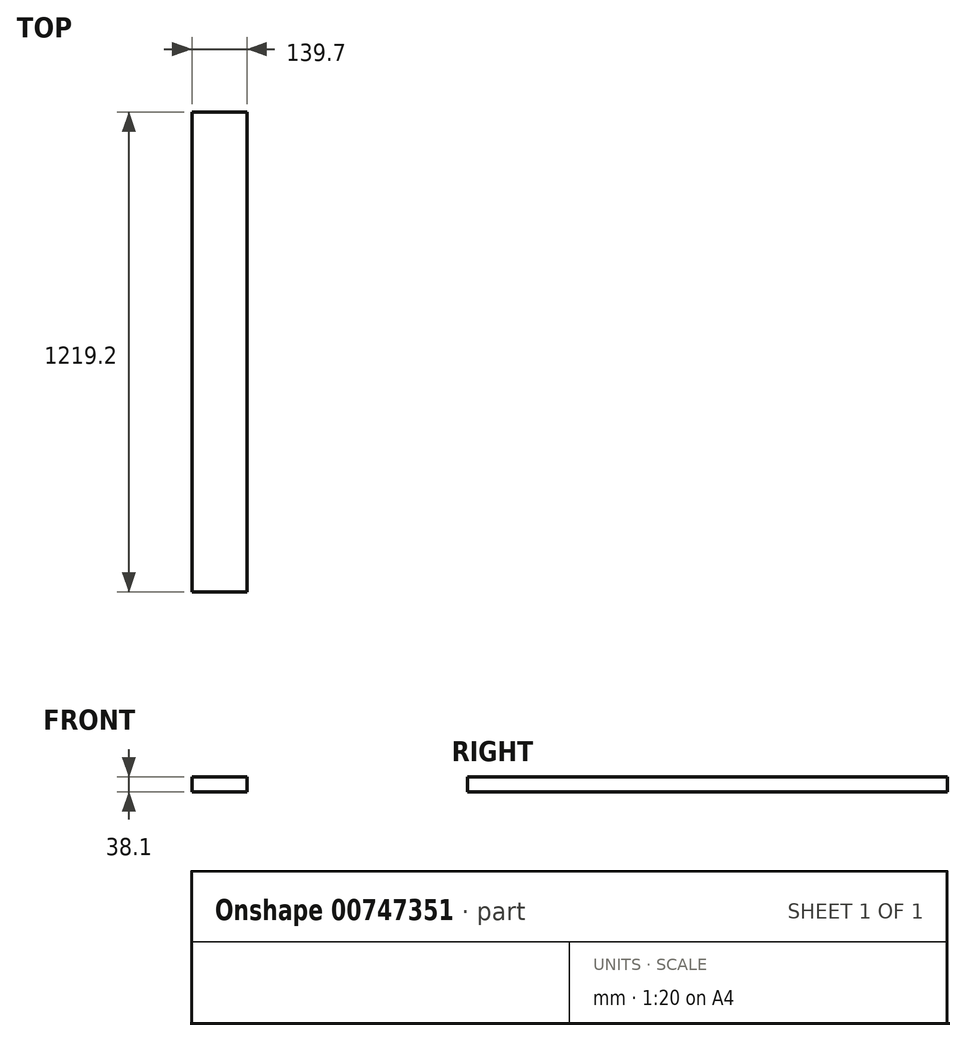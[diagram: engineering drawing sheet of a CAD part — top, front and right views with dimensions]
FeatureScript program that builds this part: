
annotation { "Feature Type Name" : "Feature", "Feature Type Description" : "" }
export const myFeature = defineFeature(function(context is Context, id is Id, definition is map)
    precondition{}
    {
        {
            var Q0;
            Q0=qCreatedBy(makeId("Front.planeOp"),FACE);
            var sketch = newSketch(context, id + "F0", { "sketchPlane" : qUnion([Q0])});
            skLineSegment(sketch, "E0.bottom", {"start": v(0, 0) * mm, "end": v(139.7, 0) * mm});
            skLineSegment(sketch, "E0.top", {"start": v(0, 38.1) * mm, "end": v(139.7, 38.1) * mm});
            skLineSegment(sketch, "E0.left", {"start": v(0, 0) * mm, "end": v(0, 38.1) * mm});
            skLineSegment(sketch, "E0.right", {"start": v(139.7, 0) * mm, "end": v(139.7, 38.1) * mm});
            skSolve(sketch);
        }
        {
            var Q0;
            Q0=qSketchRegion(id+"F0",true);
            extrude(context, id + "F1", {"entities" : qUnion([Q0]), "depth" : 1219.2 * mm, "offsetDistance" : 25.4 * mm});
        }
    });
